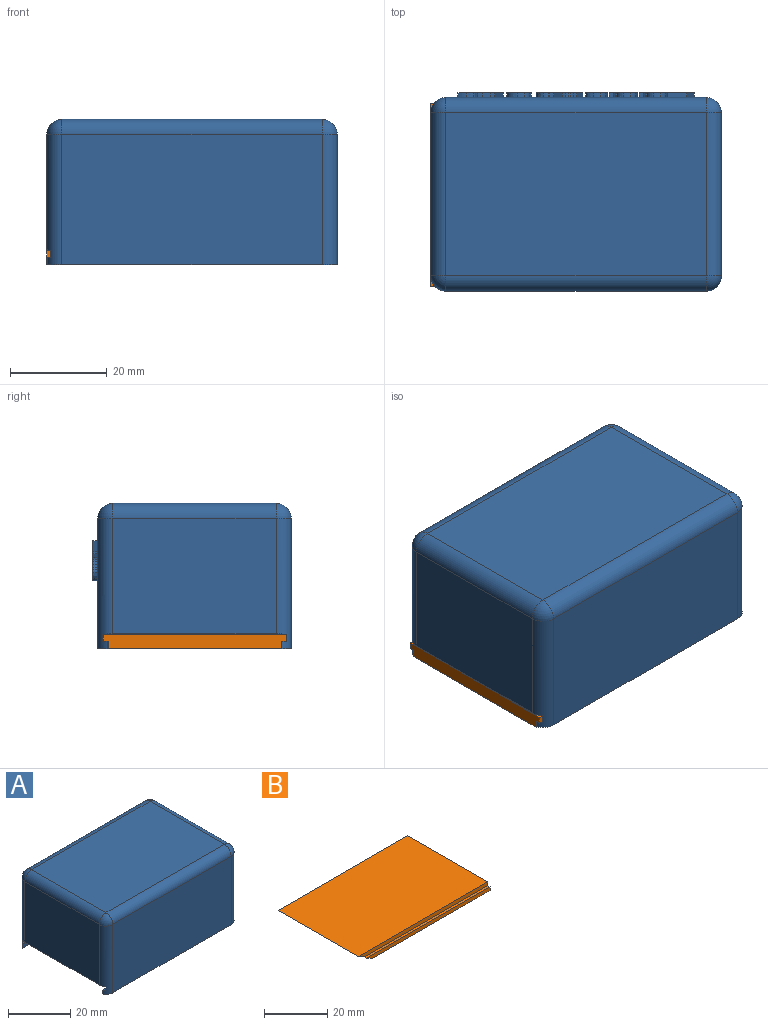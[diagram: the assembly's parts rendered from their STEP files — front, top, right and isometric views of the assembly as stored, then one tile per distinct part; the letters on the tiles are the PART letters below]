
ASSEMBLY  parts=2 mates=1
PART A: 233 faces, bbox 60x41x30 mm
  f0: plane 57.79x1.5mm, normal (0,-1,0), area 86.7mm2, adj f1,f8,f10,f28
  f1: cylinder r=3.14mm len=26.86mm, axis (0,0,1), area 127mm2, adj f0,f3,f6,f8,f11,f14,f28,f29
  f2: plane 57.79x1.5mm, normal (0,1,0), area 86.7mm2, adj f8,f10,f15,f25
  f3: plane 33.72x23.76mm, normal (-1,0,0), area 801.3mm2, adj f1,f15,f16,f31
  f4: plane 53.72x26.86mm, normal (0,-1,0), area 1443.1mm2, adj f8,f15,f21,f24
  f5: plane 33.72x26.86mm, normal (1,0,0), area 905.9mm2, adj f8,f18,f22,f24
  f6: plane 53.72x26.86mm, normal (0,1,0), area 1282.8mm2, adj f1,f8,f17,f18,f32,f33,f34,f35
  f7: plane 53.72x33.72mm, normal (0,0,1), area 1811.7mm2, adj f16,f17,f21,f22
  f8: plane 59.79x40mm, normal (0,0,-1), area 303.7mm2, adj f0,f1,f2,f4,f5,f6,f10,f15
  f9: plane 57.79x25mm, normal (0,1,0), area 1400.2mm2, adj f10,f12,f13,f15,f26,f31
  f10: plane 38x28mm, normal (-1,0,0), area 1011mm2, adj f0,f2,f8,f9,f11,f13,f25,f26
  f11: plane 57.79x25mm, normal (0,-1,0), area 1400.2mm2, adj f1,f10,f12,f13,f29,f31
  f12: plane 36x24.9mm, normal (1,0,0), area 896.4mm2, adj f9,f11,f13,f31
  f13: plane 56x36mm, normal (0,0,-1), area 2016mm2, adj f9,f10,f11,f12
  f14: sphere r=3.14mm, area 15.5mm2, adj f1,f16,f17
  f15: cylinder r=3.14mm len=26.86mm, axis (0,0,-1), area 127mm2, adj f2,f3,f4,f8,f9,f19,f25,f26
  f16: cylinder r=3.14mm len=33.72mm, axis (0,1,0), area 166.3mm2, adj f3,f7,f14,f19
  f17: cylinder r=3.14mm len=53.72mm, axis (1,0,0), area 264.8mm2, adj f6,f7,f14,f20
  f18: cylinder r=3.14mm len=26.86mm, axis (0,0,-1), area 132.4mm2, adj f5,f6,f8,f20
  f19: sphere r=3.14mm, area 15.5mm2, adj f15,f16,f21
  f20: sphere r=3.14mm, area 15.5mm2, adj f17,f18,f22
  f21: cylinder r=3.14mm len=53.72mm, axis (-1,0,0), area 264.8mm2, adj f4,f7,f19,f23
  f22: cylinder r=3.14mm len=33.72mm, axis (0,-1,0), area 166.3mm2, adj f5,f7,f20,f23
  f23: sphere r=3.14mm, area 15.5mm2, adj f21,f22,f24
  f24: cylinder r=3.14mm len=26.86mm, axis (0,0,1), area 132.4mm2, adj f4,f5,f8,f23
  f25: plane 57.79x1mm, normal (0,0,1), area 57.5mm2, adj f2,f10,f15,f27
  f26: plane 57.79x1mm, normal (0,0,-1), area 57.5mm2, adj f9,f10,f15,f27
  f27: plane 57.16x1.5mm, normal (0,1,0), area 85.7mm2, adj f10,f15,f25,f26
  f28: plane 57.79x1mm, normal (0,0,1), area 57.5mm2, adj f0,f1,f10,f30
  f29: plane 57.79x1mm, normal (0,0,-1), area 57.5mm2, adj f1,f10,f11,f30
  f30: plane 57.16x1.5mm, normal (0,-1,0), area 85.7mm2, adj f1,f10,f28,f29
  f31: plane 36x2mm, normal (0,0,-1), area 71.8mm2, adj f1,f3,f9,f11,f12,f15
  f32: plane 1x0.8mm, normal (-0.98,0,-0.21), area 0.8mm2, adj f6,f33,f43,f44
  f33: plane 2.96x1mm, normal (0,0,1), area 3mm2, adj f6,f32,f34,f44
  f34: plane 2.81x1mm, normal (-0.98,0,-0.21), area 2.9mm2, adj f6,f33,f35,f44
  f35: plane 2.78x1mm, normal (0,0,-1), area 2.8mm2, adj f6,f34,f36,f44
  f36: plane 1x0.8mm, normal (-0.98,0,-0.19), area 0.8mm2, adj f6,f35,f37,f44
  f37: plane 2.77x1mm, normal (0,0,1), area 2.8mm2, adj f6,f36,f38,f44
  f38: plane 2.46x1mm, normal (-0.98,0,-0.2), area 2.5mm2, adj f6,f37,f39,f44
  f39: plane 2.97x1mm, normal (0,0,-1), area 3mm2, adj f6,f38,f40,f44
  f40: plane 1x0.8mm, normal (-0.98,0,-0.2), area 0.8mm2, adj f6,f39,f41,f44
  f41: plane 3.86x1mm, normal (0,0,1), area 3.9mm2, adj f6,f40,f42,f44
  f42: plane 7.67x1.62mm, normal (0.98,0,0.21), area 7.8mm2, adj f6,f41,f43,f44
  f43: plane 3.86x1mm, normal (0,0,-1), area 3.9mm2, adj f6,f32,f42,f44
  f44: plane 7.67x5.48mm, normal (0,1,0), area 13.8mm2, adj f32,f33,f34,f35,f36,f37,f38,f39
  f45: extruded ~1.44x1mm, area 1.6mm2, adj f6,f46,f69,f70
  f46: extruded ~1.44x1.02mm, area 1.8mm2, adj f6,f45,f47,f70
  f47: extruded ~2.06x1mm, area 2.1mm2, adj f6,f46,f48,f70
  f48: extruded ~1.43x1mm, area 1.5mm2, adj f6,f47,f49,f70
  f49: extruded ~1.14x1mm, area 1.3mm2, adj f6,f48,f50,f70
  f50: extruded ~1x0.96mm, area 1mm2, adj f6,f49,f51,f70
  f51: extruded ~1x0.99mm, area 1.4mm2, adj f6,f50,f52,f70
  f52: plane 1x0.04mm, normal (0,0,-1), area 0mm2, adj f6,f51,f53,f70
  f53: plane 1.1x1mm, normal (0.99,0,0.11), area 1.1mm2, adj f6,f52,f54,f70
  f54: plane 1x0.73mm, normal (0,0,-1), area 0.7mm2, adj f6,f53,f55,f70
  f55: plane 8.16x1.73mm, normal (-0.98,0,-0.21), area 8.3mm2, adj f6,f54,f56,f70
  f56: plane 1x0.87mm, normal (0,0,1), area 0.9mm2, adj f6,f55,f57,f70
  f57: plane 1.88x1mm, normal (0.98,0,0.21), area 1.9mm2, adj f6,f56,f58,f70
  f58: extruded ~1.44x1mm, area 1.5mm2, adj f6,f57,f59,f70
  f59: plane 1x0.05mm, normal (0,0,1), area 0.1mm2, adj f6,f58,f69,f70
  f60: extruded ~1.19x1mm, area 1.7mm2, adj f61,f68,f70,f71
  f61: extruded ~1.65x1mm, area 1.7mm2, adj f60,f62,f70,f71
  f62: extruded ~1.22x1mm, area 1.4mm2, adj f61,f63,f70,f71
  f63: extruded ~1x0.98mm, area 1.1mm2, adj f62,f64,f70,f71
  f64: extruded ~1x0.82mm, area 0.9mm2, adj f63,f65,f70,f71
  f65: extruded ~1x0.89mm, area 1mm2, adj f64,f66,f70,f71
  f66: extruded ~1.56x1mm, area 1.6mm2, adj f65,f67,f70,f71
  f67: extruded ~1.25x1mm, area 1.5mm2, adj f66,f68,f70,f71
  f68: extruded ~1.02x1mm, area 1.2mm2, adj f60,f67,f70,f71
  f69: extruded ~1.47x1mm, area 1.9mm2, adj f6,f45,f59,f70
  f70: plane 8.27x5.88mm, normal (0,1,0), area 15.8mm2, adj f45,f46,f47,f48,f49,f50,f51,f52
  f71: plane 4.49x3.1mm, normal (0,1,0), area 10.4mm2, adj f60,f61,f62,f63,f64,f65,f66,f67
  f72: extruded ~1.44x1mm, area 1.6mm2, adj f6,f73,f96,f97
  f73: extruded ~1.44x1.02mm, area 1.8mm2, adj f6,f72,f74,f97
  f74: extruded ~2.06x1mm, area 2.1mm2, adj f6,f73,f75,f97
  f75: extruded ~1.43x1mm, area 1.5mm2, adj f6,f74,f76,f97
  f76: extruded ~1.14x1mm, area 1.3mm2, adj f6,f75,f77,f97
  f77: extruded ~1x0.96mm, area 1mm2, adj f6,f76,f78,f97
  f78: extruded ~1x0.99mm, area 1.4mm2, adj f6,f77,f79,f97
  f79: plane 1x0.04mm, normal (0,0,-1), area 0mm2, adj f6,f78,f80,f97
  f80: plane 1.1x1mm, normal (0.99,0,0.11), area 1.1mm2, adj f6,f79,f81,f97
  f81: plane 1x0.73mm, normal (0,0,-1), area 0.7mm2, adj f6,f80,f82,f97
  f82: plane 8.16x1.73mm, normal (-0.98,0,-0.21), area 8.3mm2, adj f6,f81,f83,f97
  f83: plane 1x0.87mm, normal (0,0,1), area 0.9mm2, adj f6,f82,f84,f97
  f84: plane 1.88x1mm, normal (0.98,0,0.21), area 1.9mm2, adj f6,f83,f85,f97
  f85: extruded ~1.44x1mm, area 1.5mm2, adj f6,f84,f86,f97
  f86: plane 1x0.05mm, normal (0,0,1), area 0.1mm2, adj f6,f85,f96,f97
  f87: extruded ~1.19x1mm, area 1.7mm2, adj f88,f95,f97,f98
  f88: extruded ~1.65x1mm, area 1.7mm2, adj f87,f89,f97,f98
  f89: extruded ~1.22x1mm, area 1.4mm2, adj f88,f90,f97,f98
  f90: extruded ~1x0.98mm, area 1.1mm2, adj f89,f91,f97,f98
  f91: extruded ~1x0.82mm, area 0.9mm2, adj f90,f92,f97,f98
  f92: extruded ~1x0.89mm, area 1mm2, adj f91,f93,f97,f98
  f93: extruded ~1.56x1mm, area 1.6mm2, adj f92,f94,f97,f98
  f94: extruded ~1.25x1mm, area 1.5mm2, adj f93,f95,f97,f98
  f95: extruded ~1.02x1mm, area 1.2mm2, adj f87,f94,f97,f98
  f96: extruded ~1.47x1mm, area 1.9mm2, adj f6,f72,f86,f97
  f97: plane 8.27x5.88mm, normal (0,1,0), area 15.8mm2, adj f72,f73,f74,f75,f76,f77,f78,f79
  f98: plane 4.49x3.1mm, normal (0,1,0), area 10.4mm2, adj f87,f88,f89,f90,f91,f92,f93,f94
  f99: extruded ~1x0.83mm, area 0.8mm2, adj f6,f100,f123,f124
  f100: extruded ~1x0.87mm, area 0.9mm2, adj f6,f99,f101,f124
  f101: plane 1x0.77mm, normal (-1,0,0), area 0.8mm2, adj f6,f100,f102,f124
  f102: extruded ~1x0.87mm, area 0.9mm2, adj f6,f101,f103,f124
  f103: extruded ~1x0.68mm, area 0.7mm2, adj f6,f102,f104,f124
  f104: extruded ~1x1mm, area 1.1mm2, adj f6,f103,f105,f124
  f105: extruded ~1.07x1mm, area 1.1mm2, adj f6,f104,f106,f124
  f106: plane 1x0.42mm, normal (-1,0,-0.05), area 0.4mm2, adj f6,f105,f107,f124
  f107: plane 1x0.17mm, normal (0,0,-1), area 0.2mm2, adj f6,f106,f108,f124
  f108: extruded ~2.49x1mm, area 2.6mm2, adj f6,f107,f109,f124
  f109: extruded ~1.48x1mm, area 1.8mm2, adj f6,f108,f110,f124
  f110: extruded ~1x0.97mm, area 1.1mm2, adj f6,f109,f111,f124
  f111: extruded ~1.21x1mm, area 1.3mm2, adj f6,f110,f112,f124
  f112: extruded ~1.42x1mm, area 1.5mm2, adj f6,f111,f113,f124
  f113: extruded ~1.41x1.04mm, area 1.8mm2, adj f6,f112,f114,f124
  f114: extruded ~1.89x1mm, area 1.9mm2, adj f6,f113,f115,f124
  f115: extruded ~1.58x1mm, area 1.7mm2, adj f6,f114,f123,f124
  f116: extruded ~1x0.6mm, area 0.6mm2, adj f117,f122,f124,f125
  f117: extruded ~1x0.46mm, area 0.5mm2, adj f116,f118,f124,f125
  f118: extruded ~1x0.91mm, area 1.2mm2, adj f117,f119,f124,f125
  f119: extruded ~1.83x1mm, area 1.9mm2, adj f118,f120,f124,f125
  f120: plane 1x0.06mm, normal (0,0,1), area 0.1mm2, adj f119,f121,f124,f125
  f121: extruded ~1.37x1mm, area 1.6mm2, adj f120,f122,f124,f125
  f122: extruded ~1.02x1mm, area 1.2mm2, adj f116,f121,f124,f125
  f123: extruded ~1.52x1mm, area 1.7mm2, adj f6,f99,f115,f124
  f124: plane 5.96x4.46mm, normal (0,1,0), area 11.8mm2, adj f99,f100,f101,f102,f103,f104,f105,f106
  f125: plane 2.54x1.86mm, normal (0,1,0), area 3.2mm2, adj f116,f117,f118,f119,f120,f121,f122
  f126: extruded ~1x0.6mm, area 0.6mm2, adj f6,f127,f140,f141
  f127: extruded ~1x0.52mm, area 0.6mm2, adj f6,f126,f128,f141
  f128: extruded ~1x0.72mm, area 1mm2, adj f6,f127,f129,f141
  f129: plane 1x0.05mm, normal (0,0,1), area 0.1mm2, adj f6,f128,f130,f141
  f130: plane 1.06x1mm, normal (-0.99,0,-0.11), area 1.1mm2, adj f6,f129,f131,f141
  f131: plane 1x0.73mm, normal (0,0,1), area 0.7mm2, adj f6,f130,f132,f141
  f132: plane 5.75x1.23mm, normal (0.98,0,0.21), area 5.9mm2, adj f6,f131,f133,f141
  f133: plane 1x0.88mm, normal (0,0,-1), area 0.9mm2, adj f6,f132,f134,f141
  f134: plane 2.63x1mm, normal (-0.98,0,-0.21), area 2.7mm2, adj f6,f133,f135,f141
  f135: extruded ~1.24x1mm, area 1.3mm2, adj f6,f134,f136,f141
  f136: extruded ~1x0.87mm, area 1.1mm2, adj f6,f135,f137,f141
  f137: extruded ~1x0.89mm, area 1mm2, adj f6,f136,f138,f141
  f138: extruded ~1x0.55mm, area 0.6mm2, adj f6,f137,f139,f141
  f139: plane 1x0.79mm, normal (-0.97,0,-0.23), area 0.8mm2, adj f6,f138,f140,f141
  f140: extruded ~1x0.63mm, area 0.6mm2, adj f6,f126,f139,f141
  f141: plane 5.86x4.27mm, normal (0,1,0), area 6.9mm2, adj f126,f127,f128,f129,f130,f131,f132,f133
  f142: extruded ~1.45x1mm, area 1.6mm2, adj f6,f143,f167,f168
  f143: extruded ~1.45x1mm, area 1.8mm2, adj f6,f142,f144,f168
  f144: extruded ~2.03x1mm, area 2.1mm2, adj f6,f143,f145,f168
  f145: extruded ~1.43x1mm, area 1.5mm2, adj f6,f144,f146,f168
  f146: extruded ~1.15x1mm, area 1.3mm2, adj f6,f145,f147,f168
  f147: extruded ~1x0.98mm, area 1mm2, adj f6,f146,f148,f168
  f148: extruded ~1x0.96mm, area 1.3mm2, adj f6,f147,f149,f168
  f149: plane 1x0.05mm, normal (0,0,1), area 0mm2, adj f6,f148,f150,f168
  f150: extruded ~1.58x1mm, area 1.6mm2, adj f6,f149,f151,f168
  f151: extruded ~1.94x1mm, area 2mm2, adj f6,f150,f152,f168
  f152: plane 1x0.88mm, normal (0,0,1), area 0.9mm2, adj f6,f151,f153,f168
  f153: plane 8.16x1.73mm, normal (0.98,0,0.21), area 8.3mm2, adj f6,f152,f154,f168
  f154: plane 1x0.66mm, normal (0,0,-1), area 0.7mm2, adj f6,f153,f155,f168
  f155: plane 1x0.89mm, normal (-0.92,0,-0.38), area 1mm2, adj f6,f154,f156,f168
  f156: plane 1x0.05mm, normal (0,0,-1), area 0.1mm2, adj f6,f155,f157,f168
  f157: extruded ~1x0.73mm, area 0.9mm2, adj f6,f156,f167,f168
  f158: extruded ~1.19x1mm, area 1.7mm2, adj f159,f166,f168,f169
  f159: extruded ~1.67x1mm, area 1.7mm2, adj f158,f160,f168,f169
  f160: extruded ~1.21x1mm, area 1.4mm2, adj f159,f161,f168,f169
  f161: extruded ~1x0.97mm, area 1.1mm2, adj f160,f162,f168,f169
  f162: extruded ~1x0.84mm, area 0.9mm2, adj f161,f163,f168,f169
  f163: extruded ~1x0.88mm, area 1mm2, adj f162,f164,f168,f169
  f164: extruded ~1.55x1mm, area 1.6mm2, adj f163,f165,f168,f169
  f165: extruded ~1.25x1mm, area 1.5mm2, adj f164,f166,f168,f169
  f166: extruded ~1.03x1mm, area 1.2mm2, adj f158,f165,f168,f169
  f167: extruded ~1x0.89mm, area 0.9mm2, adj f6,f142,f157,f168
  f168: plane 8.27x5.36mm, normal (0,1,0), area 15.7mm2, adj f142,f143,f144,f145,f146,f147,f148,f149
  f169: plane 4.49x3.1mm, normal (0,1,0), area 10.4mm2, adj f158,f159,f160,f161,f162,f163,f164,f165
  f170: extruded ~1.44x1mm, area 1.5mm2, adj f6,f171,f189,f190
  f171: extruded ~1.35x1.03mm, area 1.7mm2, adj f6,f170,f172,f190
  f172: extruded ~1.88x1mm, area 1.9mm2, adj f6,f171,f173,f190
  f173: extruded ~1.62x1mm, area 1.8mm2, adj f6,f172,f174,f190
  f174: extruded ~1.58x1mm, area 1.7mm2, adj f6,f173,f175,f190
  f175: extruded ~1.46x1mm, area 1.6mm2, adj f6,f174,f176,f190
  f176: extruded ~1.35x1.02mm, area 1.7mm2, adj f6,f175,f177,f190
  f177: extruded ~1.86x1mm, area 1.9mm2, adj f6,f176,f178,f190
  f178: extruded ~1.62x1mm, area 1.8mm2, adj f6,f177,f189,f190
  f179: extruded ~1.61x1mm, area 1.6mm2, adj f180,f188,f190,f191
  f180: extruded ~1.09x1mm, area 1.3mm2, adj f179,f181,f190,f191
  f181: extruded ~1x0.98mm, area 1.1mm2, adj f180,f182,f190,f191
  f182: extruded ~1x0.96mm, area 1.1mm2, adj f181,f183,f190,f191
  f183: extruded ~1.06x1mm, area 1.1mm2, adj f182,f184,f190,f191
  f184: extruded ~1.53x1mm, area 1.6mm2, adj f183,f185,f190,f191
  f185: extruded ~1.08x1mm, area 1.3mm2, adj f184,f186,f190,f191
  f186: extruded ~1.03x1mm, area 1.1mm2, adj f185,f187,f190,f191
  f187: extruded ~1x0.89mm, area 1mm2, adj f186,f188,f190,f191
  f188: extruded ~1x0.98mm, area 1.1mm2, adj f179,f187,f190,f191
  f189: extruded ~1.57x1mm, area 1.7mm2, adj f6,f170,f178,f190
  f190: plane 5.91x5.01mm, normal (0,1,0), area 12.3mm2, adj f170,f171,f172,f173,f174,f175,f176,f177
  f191: plane 4.44x3.19mm, normal (0,1,0), area 11.2mm2, adj f179,f180,f181,f182,f183,f184,f185,f186
  f192: plane 1x0.02mm, normal (0,0,1), area 0mm2, adj f6,f193,f205,f206
  f193: extruded ~2.07x1mm, area 2.1mm2, adj f6,f192,f194,f206
  f194: extruded ~3.16x1mm, area 3.2mm2, adj f6,f193,f195,f206
  f195: plane 1x0.89mm, normal (0,0,1), area 0.9mm2, adj f6,f194,f196,f206
  f196: plane 8.16x1.73mm, normal (0.98,0,0.21), area 8.3mm2, adj f6,f195,f197,f206
  f197: plane 1x0.89mm, normal (0,0,-1), area 0.9mm2, adj f6,f196,f198,f206
  f198: plane 2.1x1mm, normal (-0.98,0,-0.2), area 2.1mm2, adj f6,f197,f199,f206
  f199: plane 1x0.8mm, normal (-0.63,0,-0.78), area 1mm2, adj f6,f198,f200,f206
  f200: plane 2.75x1.23mm, normal (0.91,0,-0.41), area 3mm2, adj f6,f199,f201,f206
  f201: plane 1x0.98mm, normal (0,0,-1), area 1mm2, adj f6,f200,f202,f206
  f202: plane 3.3x1.55mm, normal (-0.91,0,0.42), area 3.6mm2, adj f6,f201,f203,f206
  f203: plane 2.46x2.45mm, normal (-0.71,0,-0.71), area 3.5mm2, adj f6,f202,f204,f206
  f204: plane 1.05x1mm, normal (0,0,1), area 1.1mm2, adj f6,f203,f205,f206
  f205: plane 2.82x2.76mm, normal (0.71,0,0.7), area 3.9mm2, adj f6,f192,f204,f206
  f206: plane 8.16x5.25mm, normal (0,1,0), area 13.3mm2, adj f192,f193,f194,f195,f196,f197,f198,f199
  f207: extruded ~1x0.59mm, area 0.6mm2, adj f6,f208,f231,f232
  f208: extruded ~1x0.49mm, area 0.6mm2, adj f6,f207,f209,f232
  f209: extruded ~1x0.81mm, area 1mm2, adj f6,f208,f210,f232
  f210: extruded ~1x0.77mm, area 0.9mm2, adj f6,f209,f211,f232
  f211: extruded ~1x0.5mm, area 0.5mm2, adj f6,f210,f212,f232
  f212: extruded ~1x0.59mm, area 0.7mm2, adj f6,f211,f213,f232
  f213: extruded ~1x0.77mm, area 0.8mm2, adj f6,f212,f214,f232
  f214: extruded ~1.16x1mm, area 1.2mm2, adj f6,f213,f215,f232
  f215: plane 1x0.29mm, normal (0.41,0,-0.91), area 0.3mm2, adj f6,f214,f216,f232
  f216: plane 1x0.72mm, normal (-0.93,0,-0.37), area 0.8mm2, adj f6,f215,f217,f232
  f217: extruded ~1.73x1mm, area 1.8mm2, adj f6,f216,f218,f232
  f218: extruded ~1.4x1mm, area 1.5mm2, adj f6,f217,f219,f232
  f219: extruded ~1.17x1mm, area 1.3mm2, adj f6,f218,f220,f232
  f220: extruded ~1x0.87mm, area 0.9mm2, adj f6,f219,f221,f232
  f221: extruded ~1x0.97mm, area 1.2mm2, adj f6,f220,f222,f232
  f222: extruded ~1x0.79mm, area 1mm2, adj f6,f221,f223,f232
  f223: extruded ~1x0.5mm, area 0.5mm2, adj f6,f222,f224,f232
  f224: extruded ~1x0.67mm, area 0.8mm2, adj f6,f223,f225,f232
  f225: extruded ~1x1mm, area 1mm2, adj f6,f224,f226,f232
  f226: extruded ~1x0.79mm, area 0.8mm2, adj f6,f225,f227,f232
  f227: extruded ~1x0.79mm, area 0.9mm2, adj f6,f226,f228,f232
  f228: plane 1x0.83mm, normal (1,0,0), area 0.8mm2, adj f6,f227,f229,f232
  f229: extruded ~1.6x1mm, area 1.7mm2, adj f6,f228,f230,f232
  f230: extruded ~1.63x1mm, area 1.7mm2, adj f6,f229,f231,f232
  f231: extruded ~1.28x1mm, area 1.5mm2, adj f6,f207,f230,f232
  f232: plane 5.96x4.34mm, normal (0,1,0), area 9.4mm2, adj f207,f208,f209,f210,f211,f212,f213,f214
PART B: 11 faces, bbox 58x37.8x2.9 mm
  f0: plane 55.19x1mm, normal (0,0,1), area 55.2mm2, adj f1,f2,f3,f10
  f1: plane 55.19x1.4mm, normal (0,-1,0), area 75.4mm2, adj f0,f3,f6,f10
  f2: plane 58x1.5mm, normal (0,-1,0), area 84.9mm2, adj f0,f3,f8,f9
  f3: plane 37.8x2.9mm, normal (1,0,0), area 106.6mm2, adj f0,f1,f2,f4,f5,f6,f7,f8
  f4: plane 55.19x1.4mm, normal (0,1,0), area 75.4mm2, adj f3,f5,f6,f10
  f5: plane 55.19x1mm, normal (0,0,1), area 55.2mm2, adj f3,f4,f7,f10
  f6: plane 52.55x37.8mm, normal (0,0,-1), area 1986.5mm2, adj f1,f3,f4,f10
  f7: plane 58x1.5mm, normal (0,1,0), area 84.9mm2, adj f3,f5,f8,f9
  f8: plane 58x35.8mm, normal (0,0,1), area 2076.4mm2, adj f2,f3,f7,f9
  f9: plane 35.8x2.82mm, normal (-0.47,0,-0.88), area 114.1mm2, adj f2,f7,f8,f10
  f10: plane 37.8x2.64mm, normal (-0.47,0,-0.88), area 112.7mm2, adj f0,f1,f4,f5,f6,f9
PLACE A t=(-12.47,1.03,10.89)mm
PLACE B rot(axis=(0,1,0),180deg) t=(-13.47,0.93,13.79)mm
MATE slider B.f8 <-> A.f8  axis (0,0,-1) through (15.53,-16.97,10.89)mm
